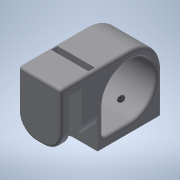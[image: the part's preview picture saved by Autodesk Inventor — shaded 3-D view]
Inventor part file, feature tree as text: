
AUTODESK INVENTOR PART (.ipt)
format: ipt  version: 2022 (Build 260153000, 153)  size: 274,432 bytes
history: native  units: mm
features: fillet x7, extrude x5, sketch x5, hole x1, chamfer x1
ambient origin geometry x8: Origin, YZ Plane, XZ Plane, XY Plane, X Axis, Y Axis, Z Axis, Center Point
bodies: Volumenkörper1 (feature_tree)
feature tree (19):
  extrude  "Extrusion1"  Depth=24.0mm
  extrude  "Extrusion2"  Depth=3.0mm
  fillet  "Rundung1"  Radius=26.0mm
  fillet  "Rundung2"  Radius=15.0mm
  fillet  "Rundung3"  Radius=15.0mm
  extrude  "Extrusion4"  Depth=15.0mm
  hole  "Bohrung2"  [1 undecoded]
  fillet  "Rundung10"  Radius=36.0mm
  fillet  "Rundung12"  Radius=40.0mm
  chamfer  "Fase1"  Distance=32.0mm
  extrude  "Extrusion5"  Depth=5.0mm
  extrude  "Extrusion6"  Depth=24.0mm
  fillet  "Rundung14"  Radius=3.6mm
  fillet  "Rundung15"  Radius=8.0mm
  sketch  "Skizze2"  dims[d2=24.0mm d3=0.0mm d4=30.0mm]
  sketch  "Skizze5"  dims[d5=30.0mm d6=3.0mm d8=26.0mm d9=0.0mm d10=15.0mm d11=15.0mm]
  sketch  "Skizze6"  dims[d12=18.0mm d36=15.0mm]
  sketch  "Skizze7"  dims[d38=1.5mm d40=0.5mm d41=2.0mm d42=45.0deg d43=36.0mm d45=40.0mm]
  sketch  "Skizze8"  dims[d46=45.0mm d47=32.0mm d49=5.0mm d50=21.0mm d51=3.6mm d52=8.0mm d53=0.0mm d55=10.8mm d56=3.242mm d57=8.0mm d58=4.0mm d59=2.0mm d60=90.0deg d61=11.8mm d62=20.594885mm d63=5.0mm d64=10.0mm d65=6.0mm d66=7.0mm d67=0.0mm d68=4.5mm d69=0.0mm d70=10.0mm d71=1.5mm d72=24.0mm d73=0.872665mm d74=0.5mm d75=0.872665mm]
note: 1 required parameter value undecoded (feature->parameter linkage not recoverable at this tier; creation-order binding heuristic only, values carry confidence <= 0.55)
